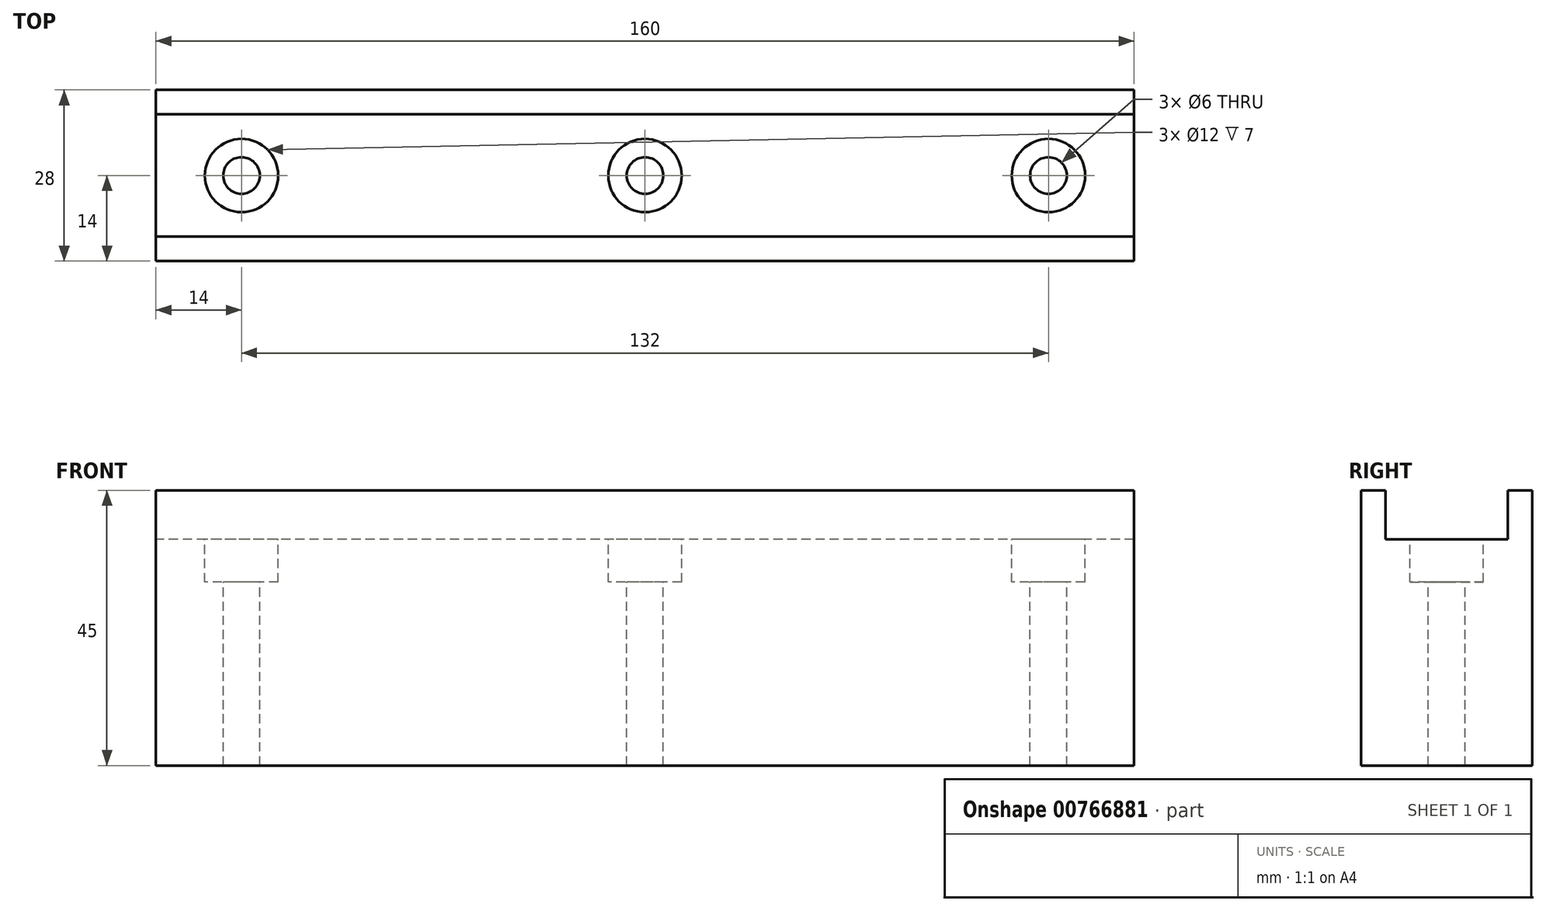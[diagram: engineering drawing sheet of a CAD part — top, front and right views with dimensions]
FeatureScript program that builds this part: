
annotation { "Feature Type Name" : "Feature", "Feature Type Description" : "" }
export const myFeature = defineFeature(function(context is Context, id is Id, definition is map)
    precondition{}
    {
        {
            var Q0;
            Q0=qCreatedBy(makeId("Right.planeOp"),FACE);
            var sketch = newSketch(context, id + "F0", { "sketchPlane" : qUnion([Q0])});
            skLineSegment(sketch, "E0", {"start": v(0, 0) * mm, "end": v(28, 0) * mm});
            skLineSegment(sketch, "E1", {"start": v(28, 0) * mm, "end": v(28, 45) * mm});
            skLineSegment(sketch, "E2", {"start": v(28, 45) * mm, "end": v(24, 45) * mm});
            skLineSegment(sketch, "E3", {"start": v(24, 45) * mm, "end": v(24, 37) * mm});
            skLineSegment(sketch, "E4", {"start": v(24, 37) * mm, "end": v(4, 37) * mm});
            skLineSegment(sketch, "E5", {"start": v(4, 37) * mm, "end": v(4, 45) * mm});
            skLineSegment(sketch, "E6", {"start": v(4, 45) * mm, "end": v(0, 45) * mm});
            skLineSegment(sketch, "E7", {"start": v(0, 45) * mm, "end": v(0, 0) * mm});
            skSolve(sketch);
        }
        {
            var Q0;
            Q0=makeQuery(id+"F0.imprint","IMPRINT",FACE,{"disambiguationData":[TD([[makeQuery(id+"F0.imprint","IMPRINT",EDGE,{"derivedFrom":sQuery(id+"F0.wireOp",EDGE,"E0")}),1.0]])]});
            extrude(context, id + "F1", {"entities" : qUnion([Q0]), "depth" : 80 * mm, "offsetDistance" : 25 * mm, "hasSecondDirection" : true, "secondDirectionOppositeDirection" : true, "secondDirectionDepth" : 80 * mm});
        }
        {
            var Q0;
            Q0=makeQuery(id+"F1.opExtrude","SWEPT_FACE",FACE,{"disambiguationData":[OSD([sQuery(id+"F0.wireOp",EDGE,"E4")])]});
            var sketch = newSketch(context, id + "F2", { "sketchPlane" : qUnion([Q0])});
            skPoint(sketch, "E8", {"position": v(-66, 14) * mm});
            skPoint(sketch, "E9", {"position": v(0, 14) * mm});
            skPoint(sketch, "E10", {"position": v(66, 14) * mm});
            skSolve(sketch);
        }
        {
            var Q0;
            Q0=sQuery(id+"F2.wireOp",VERTEX,"E8");
            var Q1;
            Q1=sQuery(id+"F2.wireOp",VERTEX,"E9");
            var Q2;
            Q2=sQuery(id+"F2.wireOp",VERTEX,"E10");
            var Q3;
            Q3=makeQuery(id+"F1.opExtrude","SWEPT_BODY",BODY,{"disambiguationData":[OSD([sQuery(id+"F0.wireOp",EDGE,"E0"),sQuery(id+"F0.wireOp",EDGE,"E1"),sQuery(id+"F0.wireOp",EDGE,"E2"),sQuery(id+"F0.wireOp",EDGE,"E3"),sQuery(id+"F0.wireOp",EDGE,"E4"),sQuery(id+"F0.wireOp",EDGE,"E5"),sQuery(id+"F0.wireOp",EDGE,"E6"),sQuery(id+"F0.wireOp",EDGE,"E7")])]});
            hole(context, id + "F3", {"style" : HoleStyle.C_BORE, "endStyle" : HoleEndStyle.BLIND, "holeDiameter" : 6 * mm, "cBoreDiameter" : 12 * mm, "cBoreDepth" : 7 * mm, "majorDiameter" : 5 * mm, "holeDepth" : 38 * mm, "isTappedThrough" : true, "tappedDepth" : 12 * mm, "tapClearance" : 3, "locations" : qUnion([Q0, Q1, Q2]), "scope" : qUnion([Q3])});
        }
    });
